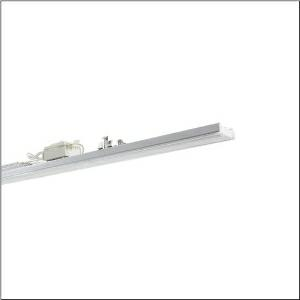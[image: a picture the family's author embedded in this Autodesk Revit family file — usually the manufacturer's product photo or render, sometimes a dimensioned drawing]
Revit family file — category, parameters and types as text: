
# Revit family: licross_r__11_recessed_mo_51te14cn485g_4836
name_source: partatom
category: Lighting Fixtures
units: mm (PartAtom-declared; Revit-internal decimal feet)

## family parameters
Cut with Voids When Loaded = No
Host = Face
Light Source = No
Part Type = Normal
Room Calculation Point = No
Round Connector Dimension = Use Diameter
Shared = No

## types (1)
- --- (1 x LED, 8570 lm, 49.3 W, 4000K)
    Apparent Load = 49 VA
    CIE Flux Codes = 56 84 97 100 100
    Color Rendering = 80
    Color Temperature = 4000K
    Default Elevation = 1800 mm
    Description = Licross® 11 Recessed MO, luminaire insert, of sheet steel, galvanised, coil coated, white, length: 1.500mm, width: 66mm, height: 67mm, LED rated luminous flux: 8.570lm, light colour: 840, control gear: ON/OFF Multilumen, CLOi, with plug, 3-pole, with phase selection, mains connection: 220..240V, AC, 50/60Hz, start of lifetime: 49W, end of service life: 55W, halogen-free wiring, primary light control with lens, of plastic, primary optical cover: cover, of PMMA, light emission: direct distribution, primary light characteristic: asymmetric, protection rating (complete): IP54, insulation class (complete): insulation class I (protective earthing), certification: CE, ENEC, VDE, UKCA, protection symbol: D if used in an environment with non-conductive dust loads with corresponding accessories, impact resistance: IK06, permissible ambient temperature for indoor applications: -35..+40°C, corresponds to IFS (International Featured Standards) requirements for safety and quality in the food industry, reducing of maximum allowable ambient temperature of 5°C with ceiling mounting, LABS conformity tested according to VDMA 24364:2018-05, packaging unit: 1 piece
    Height = 58 mm
    Lamp = 1 x LED
    Lamp Light Flux = 8570 lm
    Lamp Power = 49.3 W
    Lamp count = 1
    Length = 1500 mm
    Luminous efficacy = 174 lm/W
    Manufacturer = Siteco
    ModVariant = No
    Model = 51TE14CN485G
    Mounting Place = Ceiling
    Mounting Type = Pendant
    Number of Poles = 1
    OnlyDefault = Yes
    Power Factor = 1
    Product Name = Licross® 11 Recessed MO
    Product group = luminaire insert
    ProductGroupID = 902
    Protection Class = Protection class I
    Protection Degree = IP 54
    RLX_Detail_Level = 1
    RLX_Emergency_Light_Flux = 0 lm
    RLX_Emergency_Type = 0
    RLX_Emergency_Type_DB = No
    RlxData = <blob elided: 22801 chars, md5=78b986a7>
    Socket = socket
    Standby Power = 0 W
    System Light Flux = 8570 lm
    System Power = 49 W
    Type Comments = factory setting: luminous flux: 100 % | (A | C | E) | 113 mA
    Type Image = l_1296930.jpg
    URL = http://relux.com
    VarID = @adj_085206
    Voltage = 0 V
    Weight = 0.00 kg
    Width = 66 mm

## geometry (parser evidence)
native form markers: Blend x4, Sweep x10
no freeform markers — native parametric forms only
